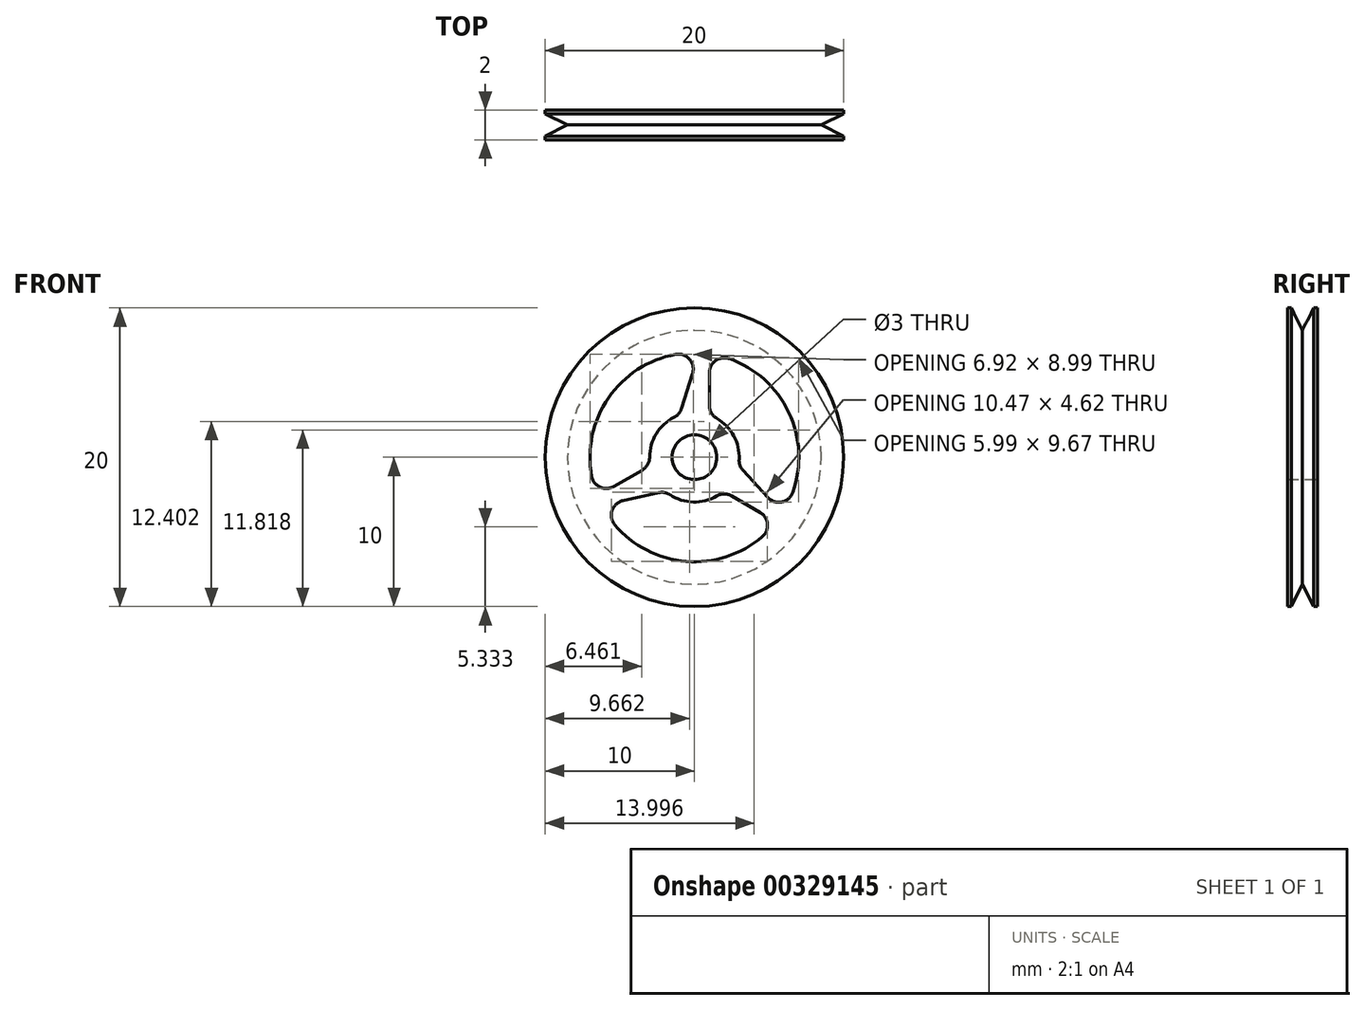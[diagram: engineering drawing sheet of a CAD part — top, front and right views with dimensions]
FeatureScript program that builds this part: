
annotation { "Feature Type Name" : "Feature", "Feature Type Description" : "" }
export const myFeature = defineFeature(function(context is Context, id is Id, definition is map)
    precondition{}
    {
        {
            var Q0;
            Q0=qCreatedBy(makeId("Front.planeOp"),FACE);
            var sketch = newSketch(context, id + "F0", { "sketchPlane" : qUnion([Q0])});
            skCircle(sketch, "E0", {"center": v(0, 0) * mm, "radius": 10 * mm});
            skArc(sketch, "E1.0", {"start": v(-1.26, 6.89) * mm, "mid": v(-5.76, 3.97) * mm, "end": v(-6.88, -1.28) * mm});
            skArc(sketch, "E2", {"start": v(-1.36, 2.67) * mm, "mid": v(-2.56, 1.57) * mm, "end": v(-3, 0) * mm});
            skCircle(sketch, "E3", {"center": v(0, 0) * mm, "radius": 1.5 * mm});
            skLineSegment(sketch, "E4.trimOffspring", {"start": v(1, 5.66) * mm, "end": v(1, 3.46) * mm});
            skLineSegment(sketch, "E5.trimOffspring", {"start": v(-0.12, 5.6) * mm, "end": v(-0.86, 3.26) * mm});
            skLineSegment(sketch, "E6.1.0", {"start": v(-4.79, -2.9) * mm, "end": v(-2.4, -2.38) * mm});
            skLineSegment(sketch, "E6.1.1", {"start": v(-5.4, -1.96) * mm, "end": v(-3.5, -0.87) * mm});
            skLineSegment(sketch, "E6.2.0", {"start": v(4.91, -2.7) * mm, "end": v(3.26, -0.88) * mm});
            skLineSegment(sketch, "E6.2.1", {"start": v(4.4, -3.7) * mm, "end": v(2.5, -2.6) * mm});
            skPoint(sketch, "E7.orphan", {"position": v(0, 10) * mm});
            skArc(sketch, "E8.trimOffspring", {"start": v(-1.63, -2.52) * mm, "mid": v(-0.08, -3) * mm, "end": v(1.5, -2.6) * mm});
            skArc(sketch, "E9.trimOffspring", {"start": v(-5.33, -4.53) * mm, "mid": v(-0.56, -6.98) * mm, "end": v(4.55, -5.32) * mm});
            skArc(sketch, "E10.trimOffspring", {"start": v(3, -0.16) * mm, "mid": v(2.64, 1.43) * mm, "end": v(1.5, 2.6) * mm});
            skArc(sketch, "E11.trimOffspring", {"start": v(6.6, -2.35) * mm, "mid": v(6.32, 3) * mm, "end": v(2.33, 6.6) * mm});
            skPoint(sketch, "E12.visualSharp", {"position": v(0.31, 7) * mm});
            skArc(sketch, "E12.filletArc", {"start": v(-0.12, 5.6) * mm, "mid": v(-0.33, 6.56) * mm, "end": v(-1.26, 6.89) * mm});
            skPoint(sketch, "E13.visualSharp", {"position": v(-1, 2.83) * mm});
            skArc(sketch, "E13.filletArc", {"start": v(-1.36, 2.67) * mm, "mid": v(-1.05, 2.92) * mm, "end": v(-0.86, 3.26) * mm});
            skPoint(sketch, "E14.visualSharp", {"position": v(-2.95, -0.55) * mm});
            skArc(sketch, "E14.filletArc", {"start": v(-3.5, -0.87) * mm, "mid": v(-3.13, -0.5) * mm, "end": v(-3, 0) * mm});
            skPoint(sketch, "E15.visualSharp", {"position": v(-6.5, -2.6) * mm});
            skArc(sketch, "E15.filletArc", {"start": v(-6.88, -1.28) * mm, "mid": v(-6.32, -2) * mm, "end": v(-5.4, -1.96) * mm});
            skPoint(sketch, "E16.visualSharp", {"position": v(-6.21, -3.22) * mm});
            skArc(sketch, "E16.filletArc", {"start": v(-4.79, -2.9) * mm, "mid": v(-5.52, -3.57) * mm, "end": v(-5.33, -4.53) * mm});
            skPoint(sketch, "E17.visualSharp", {"position": v(-1.95, -2.28) * mm});
            skArc(sketch, "E17.filletArc", {"start": v(-1.63, -2.52) * mm, "mid": v(-2, -2.37) * mm, "end": v(-2.4, -2.38) * mm});
            skPoint(sketch, "E18.visualSharp", {"position": v(1.95, -2.28) * mm});
            skArc(sketch, "E18.filletArc", {"start": v(2.5, -2.6) * mm, "mid": v(2, -2.46) * mm, "end": v(1.5, -2.6) * mm});
            skPoint(sketch, "E19.visualSharp", {"position": v(5.5, -4.33) * mm});
            skArc(sketch, "E19.filletArc", {"start": v(4.55, -5.32) * mm, "mid": v(4.9, -4.47) * mm, "end": v(4.4, -3.7) * mm});
            skPoint(sketch, "E20.visualSharp", {"position": v(2.95, -0.55) * mm});
            skArc(sketch, "E20.filletArc", {"start": v(3, -0.16) * mm, "mid": v(3.05, -0.55) * mm, "end": v(3.26, -0.88) * mm});
            skPoint(sketch, "E21.visualSharp", {"position": v(5.9, -3.77) * mm});
            skArc(sketch, "E21.filletArc", {"start": v(4.91, -2.7) * mm, "mid": v(5.85, -3) * mm, "end": v(6.6, -2.35) * mm});
            skPoint(sketch, "E22.visualSharp", {"position": v(1, 6.93) * mm});
            skArc(sketch, "E22.filletArc", {"start": v(2.33, 6.6) * mm, "mid": v(1.42, 6.47) * mm, "end": v(1, 5.66) * mm});
            skPoint(sketch, "E23.visualSharp", {"position": v(1, 2.83) * mm});
            skArc(sketch, "E23.filletArc", {"start": v(1, 3.46) * mm, "mid": v(1.13, 2.96) * mm, "end": v(1.5, 2.6) * mm});
            skSolve(sketch);
        }
        {
            var Q0;
            Q0=makeQuery(id+"F0.imprint","IMPRINT",FACE,{"disambiguationData":[TD([[makeQuery(id+"F0.imprint","IMPRINT",EDGE,{"derivedFrom":sQuery(id+"F0.wireOp",EDGE,"E0")}),1.0]])]});
            extrude(context, id + "F1", {"entities" : qUnion([Q0]), "depth" : 2 * mm});
        }
        {
            var Q0;
            Q0=qCreatedBy(makeId("Right.planeOp"),FACE);
            var sketch = newSketch(context, id + "F2", { "sketchPlane" : qUnion([Q0])});
            skLineSegment(sketch, "E24", {"start": v(-1, 10) * mm, "end": v(-1, 8.5) * mm});
            skLineSegment(sketch, "E25", {"start": v(-1.75, 10) * mm, "end": v(-1, 10) * mm});
            skLineSegment(sketch, "E26", {"start": v(-1.75, 10) * mm, "end": v(-1, 8.5) * mm});
            skLineSegment(sketch, "E27.MirrorCS", {"start": v(-0.25, 10) * mm, "end": v(-1, 10) * mm});
            skLineSegment(sketch, "E28.MirrorCS", {"start": v(-0.25, 10) * mm, "end": v(-1, 8.5) * mm});
            skLineSegment(sketch, "E29", {"start": v(-28.5, 0) * mm, "end": v(24.62, 0) * mm, "construction": true});
            skSolve(sketch);
        }
        {
            var Q0;
            Q0 = qSketchRegion(id + "F2", true);
            var Q1;
            Q1=sQuery(id+"F2.wireOp",EDGE,"E29");
            revolve(context, id + "F3", {"operationType" : NewBodyOperationType.REMOVE, "entities" : qUnion([Q0]), "axis" : qUnion([Q1]), "revolveType" : RevolveType.FULL, "oppositeDirection" : true});
        }
    });
